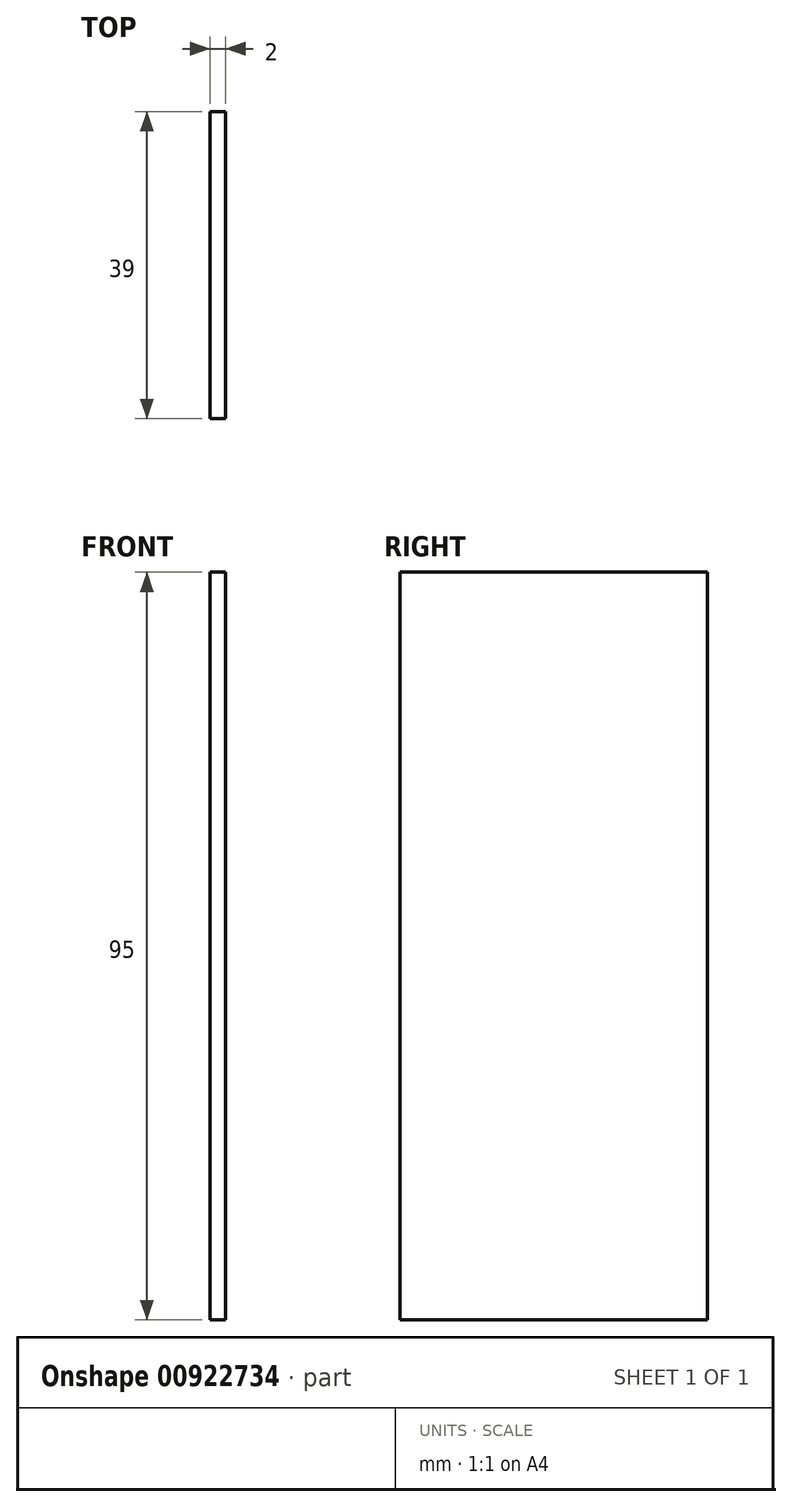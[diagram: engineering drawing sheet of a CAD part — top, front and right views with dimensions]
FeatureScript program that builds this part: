
annotation { "Feature Type Name" : "Feature", "Feature Type Description" : "" }
export const myFeature = defineFeature(function(context is Context, id is Id, definition is map)
    precondition{}
    {
        {
            var Q0;
            Q0=qCreatedBy(makeId("Right.planeOp"),FACE);
            var sketch = newSketch(context, id + "F0", { "sketchPlane" : qUnion([Q0])});
            skLineSegment(sketch, "E0.bottom", {"start": v(19.5, -47.5) * mm, "end": v(-19.5, -47.5) * mm});
            skLineSegment(sketch, "E0.top", {"start": v(19.5, 47.5) * mm, "end": v(-19.5, 47.5) * mm});
            skLineSegment(sketch, "E0.left", {"start": v(19.5, -47.5) * mm, "end": v(19.5, 47.5) * mm});
            skLineSegment(sketch, "E0.right", {"start": v(-19.5, -47.5) * mm, "end": v(-19.5, 47.5) * mm});
            skPoint(sketch, "E0.middle", {"position": v(0, 0) * mm});
            skSolve(sketch);
        }
        {
            var Q0;
            Q0 = qSketchRegion(id + "F0", true);
            extrude(context, id + "F1", {"entities" : qUnion([Q0]), "endBound" : BoundingType.SYMMETRIC, "depth" : 2 * mm, "offsetDistance" : 25 * mm});
        }
    });
